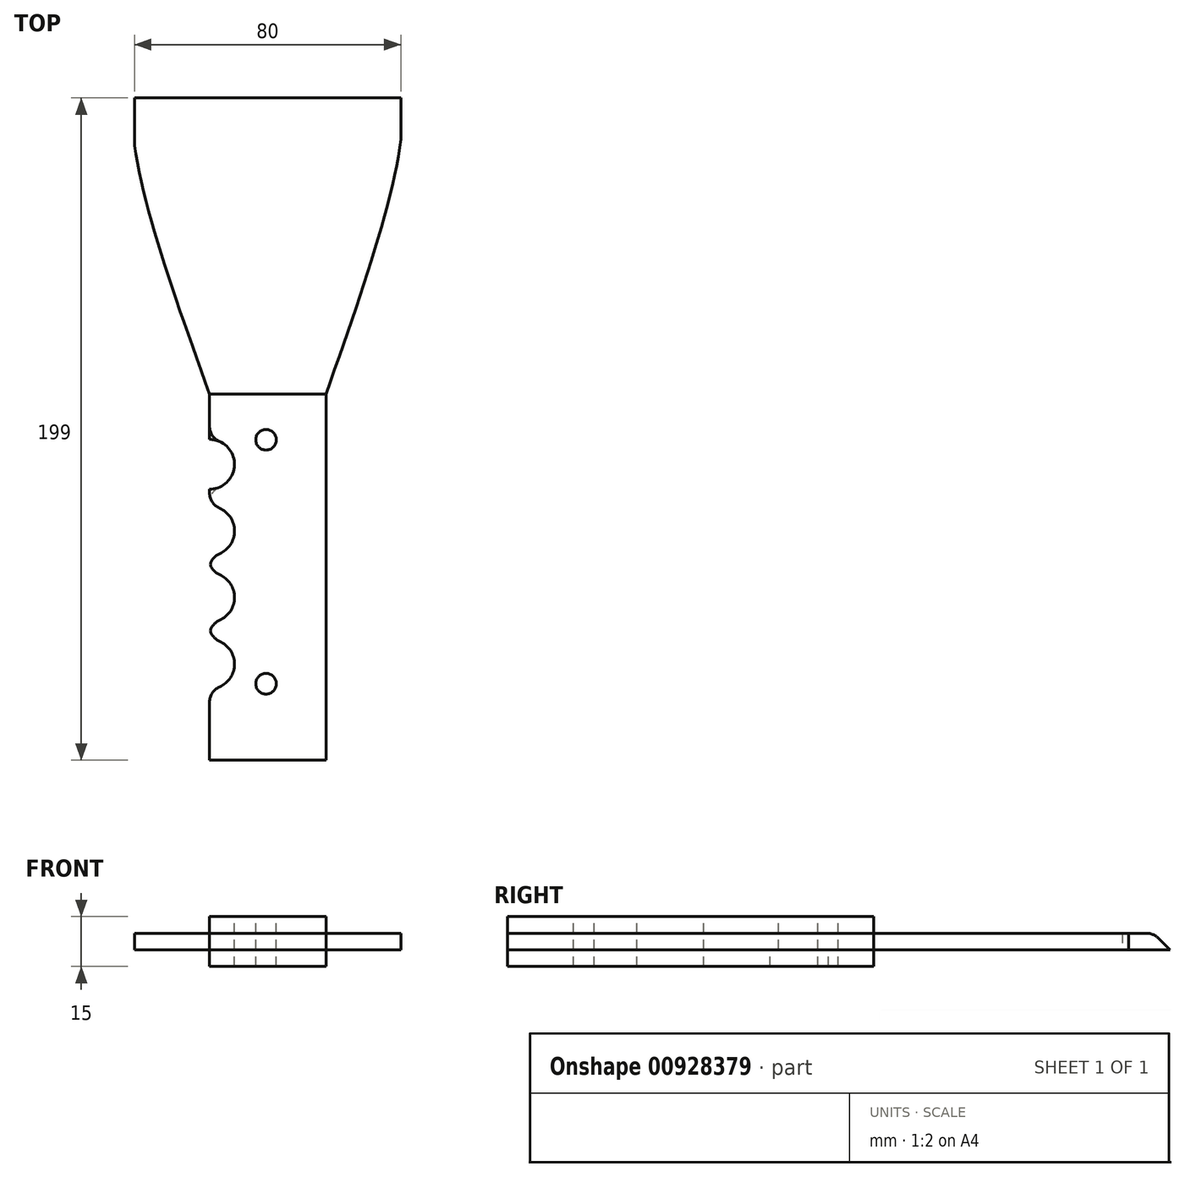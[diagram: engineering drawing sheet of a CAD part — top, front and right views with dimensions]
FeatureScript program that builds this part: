
annotation { "Feature Type Name" : "Feature", "Feature Type Description" : "" }
export const myFeature = defineFeature(function(context is Context, id is Id, definition is map)
    precondition{}
    {
        {
            var Q0;
            Q0=qCreatedBy(makeId("Top.planeOp"),FACE);
            var sketch = newSketch(context, id + "F0", { "sketchPlane" : qUnion([Q0])});
            skLineSegment(sketch, "E0.bottom", {"start": v(-27.36, -68.88) * mm, "end": v(52.64, -68.88) * mm});
            skLineSegment(sketch, "E0.top", {"start": v(-27.36, 131.12) * mm, "end": v(52.64, 131.12) * mm});
            skLineSegment(sketch, "E0.left", {"start": v(-27.36, -68.88) * mm, "end": v(-27.36, 131.12) * mm});
            skLineSegment(sketch, "E0.right", {"start": v(52.64, -68.88) * mm, "end": v(52.64, 131.12) * mm});
            skLineSegment(sketch, "E1.0", {"start": v(-27.36, 41.12) * mm, "end": v(52.64, 41.12) * mm});
            skLineSegment(sketch, "E2.0", {"start": v(30.14, -68.88) * mm, "end": v(30.14, 131.12) * mm});
            skLineSegment(sketch, "E3.0", {"start": v(-4.86, -68.88) * mm, "end": v(-4.86, 131.12) * mm});
            skFitSpline(sketch, "E4", {"points": [v(30.14, 41.12) * mm, v(52.64, 131.12) * mm, v(41.94, 146.37) * mm], "startDerivative": vector(55.76, 158.3) * mm, "endDerivative": vector(-44.94, 36.74) * mm});
            skFitSpline(sketch, "E5", {"points": [v(-4.86, 41.12) * mm, v(-27.36, 131.12) * mm, v(-15.18, 146.37) * mm], "startDerivative": vector(-57.35, 159.66) * mm, "endDerivative": vector(50, 35.48) * mm});
            skSolve(sketch);
        }
        {
            var Q0;
            {var subQ2=sQuery(id+"F0.wireOp",EDGE,"E0.top");var subQ4=sQuery(id+"F0.wireOp",EDGE,"E3.0");var subQ5=makeQuery(id+"F0.imprint","INTERSECT",VERTEX,{"derivedFrom":[subQ2,subQ4]});Q0=makeQuery(id+"F0.imprint","IMPRINT",FACE,{"disambiguationData":[TD([[makeQuery(id+"F0.imprint","IMPRINT",EDGE,{"disambiguationData":[TD([[subQ5,1.0]])],"derivedFrom":subQ2}),-1.0]])]});}
            var Q1;
            {var subQ0=sQuery(id+"F0.wireOp",EDGE,"E2.0");var subQ1=sQuery(id+"F0.wireOp",EDGE,"E0.top");var subQ2=makeQuery(id+"F0.imprint","INTERSECT",VERTEX,{"derivedFrom":[subQ1,subQ0]});Q1=makeQuery(id+"F0.imprint","IMPRINT",FACE,{"disambiguationData":[TD([[makeQuery(id+"F0.imprint","IMPRINT",EDGE,{"disambiguationData":[TD([[subQ2,1.0]])],"derivedFrom":subQ1}),-1.0]])]});}
            var Q2;
            {var subQ2=sQuery(id+"F0.wireOp",EDGE,"E0.top");var subQ4=sQuery(id+"F0.wireOp",EDGE,"E2.0");var subQ5=makeQuery(id+"F0.imprint","INTERSECT",VERTEX,{"derivedFrom":[subQ2,subQ4]});Q2=makeQuery(id+"F0.imprint","IMPRINT",FACE,{"disambiguationData":[TD([[makeQuery(id+"F0.imprint","IMPRINT",EDGE,{"disambiguationData":[TD([[subQ5,-1.0]])],"derivedFrom":subQ2}),-1.0]])]});}
            var Q3;
            {var subQ0=sQuery(id+"F0.wireOp",EDGE,"E2.0");var subQ1=sQuery(id+"F0.wireOp",EDGE,"E0.bottom");var subQ2=makeQuery(id+"F0.imprint","INTERSECT",VERTEX,{"derivedFrom":[subQ1,subQ0]});Q3=makeQuery(id+"F0.imprint","IMPRINT",FACE,{"disambiguationData":[TD([[makeQuery(id+"F0.imprint","IMPRINT",EDGE,{"disambiguationData":[TD([[subQ2,1.0]])],"derivedFrom":subQ1}),1.0]])]});}
            extrude(context, id + "F1", {"entities" : qUnion([Q0, Q1, Q2, Q3]), "depth" : 5 * mm, "offsetDistance" : 25 * mm});
        }
        {
            var Q0;
            Q0=makeQuery(id+"F1.opExtrude","CAP_FACE",FACE,{"disambiguationData":[OSD([sQuery(id+"F0.wireOp",EDGE,"E0.bottom"),sQuery(id+"F0.wireOp",EDGE,"E0.top"),sQuery(id+"F0.wireOp",EDGE,"E0.left"),sQuery(id+"F0.wireOp",EDGE,"E0.right"),sQuery(id+"F0.wireOp",EDGE,"E2.0"),sQuery(id+"F0.wireOp",EDGE,"E3.0"),sQuery(id+"F0.wireOp",EDGE,"E4"),sQuery(id+"F0.wireOp",EDGE,"E5")])],"isStart":false});
            var sketch = newSketch(context, id + "F2", { "sketchPlane" : qUnion([Q0])});
            skLineSegment(sketch, "E6", {"start": v(-4.86, 41.12) * mm, "end": v(30.14, 41.12) * mm});
            skSolve(sketch);
        }
        {
            var Q0;
            Q0=makeQuery(id+"F1.opExtrude","CAP_FACE",FACE,{"disambiguationData":[OSD([sQuery(id+"F0.wireOp",EDGE,"E0.bottom"),sQuery(id+"F0.wireOp",EDGE,"E0.top"),sQuery(id+"F0.wireOp",EDGE,"E0.left"),sQuery(id+"F0.wireOp",EDGE,"E0.right"),sQuery(id+"F0.wireOp",EDGE,"E2.0"),sQuery(id+"F0.wireOp",EDGE,"E3.0"),sQuery(id+"F0.wireOp",EDGE,"E4"),sQuery(id+"F0.wireOp",EDGE,"E5")])],"isStart":true});
            var sketch = newSketch(context, id + "F3", { "sketchPlane" : qUnion([Q0])});
            skLineSegment(sketch, "E7", {"start": v(30.14, -41.12) * mm, "end": v(-4.86, -41.12) * mm});
            skSolve(sketch);
        }
        {
            var Q0;
            Q0=makeQuery(id+"F2.imprint","IMPRINT",FACE,{"disambiguationData":[TD([[makeQuery(id+"F2.imprint","IMPRINT",EDGE,{"derivedFrom":sQuery(id+"F2.wireOp",EDGE,"E6")}),-1.0]])]});
            extrude(context, id + "F4", {"entities" : qUnion([Q0]), "depth" : 5 * mm, "offsetDistance" : 25 * mm});
        }
        {
            var Q0;
            Q0=makeQuery(id+"F3.imprint","IMPRINT",FACE,{"disambiguationData":[TD([[makeQuery(id+"F3.imprint","IMPRINT",EDGE,{"derivedFrom":sQuery(id+"F3.wireOp",EDGE,"E7")}),-1.0]])]});
            extrude(context, id + "F5", {"entities" : qUnion([Q0]), "depth" : 5 * mm, "offsetDistance" : 25 * mm});
        }
        {
            var Q0;
            Q0=makeQuery(id+"F4.opExtrude","CAP_FACE",FACE,{"disambiguationData":[OSD([sQuery(id+"F0.wireOp",EDGE,"E0.bottom"),sQuery(id+"F0.wireOp",EDGE,"E2.0"),sQuery(id+"F0.wireOp",EDGE,"E3.0"),sQuery(id+"F2.wireOp",EDGE,"E6")])],"isStart":false});
            var sketch = newSketch(context, id + "F6", { "sketchPlane" : qUnion([Q0])});
            skCircle(sketch, "E8", {"center": v(-4.86, 20) * mm, "radius": 7.5 * mm});
            skCircle(sketch, "E9", {"center": v(-4.86, 0) * mm, "radius": 7.5 * mm});
            skCircle(sketch, "E10", {"center": v(-4.86, -20) * mm, "radius": 7.5 * mm});
            skCircle(sketch, "E11", {"center": v(-4.86, -40) * mm, "radius": 7.5 * mm});
            skSolve(sketch);
        }
        {
            var Q0;
            {var subQ0=sQuery(id+"F6.wireOp",EDGE,"E8");var subQ1=makeQuery(id+"F4.opExtrude","CAP_EDGE",EDGE,{"disambiguationData":[OSD([sQuery(id+"F0.wireOp",EDGE,"E3.0")])],"isStart":false});var subQ2=makeQuery(id+"F6.imprint","INTERSECT",VERTEX,{"disambiguationData":[OD(0.0)],"derivedFrom":[subQ1,subQ0]});Q0=makeQuery(id+"F6.imprint","IMPRINT",FACE,{"disambiguationData":[TD([[makeQuery(id+"F6.imprint","IMPRINT",EDGE,{"disambiguationData":[TD([[subQ2,1.0]])],"derivedFrom":subQ0}),1.0]])]});}
            extrude(context, id + "F7", {"entities" : qUnion([Q0]), "operationType" : NewBodyOperationType.REMOVE, "oppositeDirection" : true, "depth" : 25 * mm, "offsetDistance" : 25 * mm});
        }
        {
            var Q0;
            Q0 = qSketchRegion(id + "F6", true);
            extrude(context, id + "F8", {"entities" : qUnion([Q0]), "operationType" : NewBodyOperationType.REMOVE, "oppositeDirection" : true, "depth" : 25 * mm, "offsetDistance" : 25 * mm});
        }
        {
            var Q0;
            {var subQ0=sQuery(id+"F0.wireOp",EDGE,"E3.0");var subQ1=sQuery(id+"F6.wireOp",EDGE,"E8");Q0=makeQuery(id+"F7.boolean.opBoolean","COPY",EDGE,{"disambiguationData":[topologyDisambiguationEdgeConnected([makeQuery(id+"F5.opExtrude","SWEPT_FACE",FACE,{"disambiguationData":[OSD([subQ0])]})])],"derivedFrom":makeQuery(id+"F7.opExtrude","SWEPT_EDGE",EDGE,{"disambiguationData":[OSD([subQ0,subQ1]),TDD([makeQuery(id+"F6.imprint","INTERSECT",VERTEX,{"disambiguationData":[OD(0.0)],"derivedFrom":[makeQuery(id+"F4.opExtrude","CAP_EDGE",EDGE,{"disambiguationData":[OSD([subQ0])],"isStart":false}),subQ1]})])]})});}
            var Q1;
            {var subQ0=sQuery(id+"F0.wireOp",EDGE,"E3.0");var subQ1=sQuery(id+"F6.wireOp",EDGE,"E8");Q1=makeQuery(id+"F7.boolean.opBoolean","COPY",EDGE,{"disambiguationData":[topologyDisambiguationEdgeConnected([makeQuery(id+"F1.opExtrude","SWEPT_FACE",FACE,{"disambiguationData":[OSD([subQ0])]})])],"derivedFrom":makeQuery(id+"F7.opExtrude","SWEPT_EDGE",EDGE,{"disambiguationData":[OSD([subQ0,subQ1]),TDD([makeQuery(id+"F6.imprint","INTERSECT",VERTEX,{"disambiguationData":[OD(0.0)],"derivedFrom":[makeQuery(id+"F4.opExtrude","CAP_EDGE",EDGE,{"disambiguationData":[OSD([subQ0])],"isStart":false}),subQ1]})])]})});}
            var Q2;
            {var subQ0=sQuery(id+"F0.wireOp",EDGE,"E3.0");var subQ1=sQuery(id+"F6.wireOp",EDGE,"E8");Q2=makeQuery(id+"F7.boolean.opBoolean","COPY",EDGE,{"disambiguationData":[topologyDisambiguationEdgeConnected([makeQuery(id+"F4.opExtrude","SWEPT_FACE",FACE,{"disambiguationData":[OSD([subQ0])]})])],"derivedFrom":makeQuery(id+"F7.opExtrude","SWEPT_EDGE",EDGE,{"disambiguationData":[OSD([subQ0,subQ1]),TDD([makeQuery(id+"F6.imprint","INTERSECT",VERTEX,{"disambiguationData":[OD(0.0)],"derivedFrom":[makeQuery(id+"F4.opExtrude","CAP_EDGE",EDGE,{"disambiguationData":[OSD([subQ0])],"isStart":false}),subQ1]})])]})});}
            var Q3;
            {var subQ0=sQuery(id+"F0.wireOp",EDGE,"E3.0");var subQ1=sQuery(id+"F6.wireOp",EDGE,"E8");Q3=makeQuery(id+"F7.boolean.opBoolean","COPY",EDGE,{"disambiguationData":[topologyDisambiguationEdgeConnected([makeQuery(id+"F1.opExtrude","SWEPT_FACE",FACE,{"disambiguationData":[OSD([subQ0])]})])],"derivedFrom":makeQuery(id+"F7.opExtrude","SWEPT_EDGE",EDGE,{"disambiguationData":[OSD([subQ0,subQ1]),TDD([makeQuery(id+"F6.imprint","INTERSECT",VERTEX,{"disambiguationData":[OD(1.0)],"derivedFrom":[makeQuery(id+"F4.opExtrude","CAP_EDGE",EDGE,{"disambiguationData":[OSD([subQ0])],"isStart":false}),subQ1]})])]})});}
            var Q4;
            {var subQ0=sQuery(id+"F0.wireOp",EDGE,"E3.0");var subQ1=sQuery(id+"F6.wireOp",EDGE,"E8");Q4=makeQuery(id+"F7.boolean.opBoolean","COPY",EDGE,{"disambiguationData":[topologyDisambiguationEdgeConnected([makeQuery(id+"F4.opExtrude","SWEPT_FACE",FACE,{"disambiguationData":[OSD([subQ0])]})])],"derivedFrom":makeQuery(id+"F7.opExtrude","SWEPT_EDGE",EDGE,{"disambiguationData":[OSD([subQ0,subQ1]),TDD([makeQuery(id+"F6.imprint","INTERSECT",VERTEX,{"disambiguationData":[OD(1.0)],"derivedFrom":[makeQuery(id+"F4.opExtrude","CAP_EDGE",EDGE,{"disambiguationData":[OSD([subQ0])],"isStart":false}),subQ1]})])]})});}
            var Q5;
            {var subQ0=sQuery(id+"F0.wireOp",EDGE,"E3.0");var subQ1=sQuery(id+"F6.wireOp",EDGE,"E8");Q5=makeQuery(id+"F7.boolean.opBoolean","COPY",EDGE,{"disambiguationData":[topologyDisambiguationEdgeConnected([makeQuery(id+"F5.opExtrude","SWEPT_FACE",FACE,{"disambiguationData":[OSD([subQ0])]})])],"derivedFrom":makeQuery(id+"F7.opExtrude","SWEPT_EDGE",EDGE,{"disambiguationData":[OSD([subQ0,subQ1]),TDD([makeQuery(id+"F6.imprint","INTERSECT",VERTEX,{"disambiguationData":[OD(1.0)],"derivedFrom":[makeQuery(id+"F4.opExtrude","CAP_EDGE",EDGE,{"disambiguationData":[OSD([subQ0])],"isStart":false}),subQ1]})])]})});}
            var Q6;
            {var subQ1=sQuery(id+"F0.wireOp",EDGE,"E3.0");var subQ3=sQuery(id+"F0.wireOp",EDGE,"E0.bottom");Q6=makeQuery(id+"F8.boolean.opBoolean","INTERSECT",EDGE,{"disambiguationData":[OD(0.0)],"derivedFrom":[makeQuery(id+"F7.boolean.opBoolean","SPLIT",FACE,{"disambiguationData":[TD([makeQuery(id+"F5.opExtrude","SWEPT_FACE",FACE,{"disambiguationData":[OSD([subQ3])]})])],"derivedFrom":makeQuery(id+"F5.opExtrude","SWEPT_FACE",FACE,{"disambiguationData":[OSD([subQ1])]})}),makeQuery(id+"F8.opExtrude","SWEPT_FACE",FACE,{"disambiguationData":[OSD([sQuery(id+"F6.wireOp",EDGE,"E9")])]})]});}
            var Q7;
            {var subQ0=sQuery(id+"F0.wireOp",EDGE,"E0.bottom");var subQ3=sQuery(id+"F0.wireOp",EDGE,"E3.0");Q7=makeQuery(id+"F8.boolean.opBoolean","INTERSECT",EDGE,{"disambiguationData":[OD(0.0)],"derivedFrom":[makeQuery(id+"F7.boolean.opBoolean","SPLIT",FACE,{"disambiguationData":[TD([makeQuery(id+"F1.opExtrude","SWEPT_FACE",FACE,{"disambiguationData":[OSD([subQ0])]})])],"derivedFrom":makeQuery(id+"F1.opExtrude","SWEPT_FACE",FACE,{"disambiguationData":[OSD([subQ3])]})}),makeQuery(id+"F8.opExtrude","SWEPT_FACE",FACE,{"disambiguationData":[OSD([sQuery(id+"F6.wireOp",EDGE,"E9")])]})]});}
            var Q8;
            {var subQ1=sQuery(id+"F0.wireOp",EDGE,"E3.0");var subQ3=sQuery(id+"F0.wireOp",EDGE,"E0.bottom");Q8=makeQuery(id+"F8.boolean.opBoolean","INTERSECT",EDGE,{"disambiguationData":[OD(0.0)],"derivedFrom":[makeQuery(id+"F7.boolean.opBoolean","SPLIT",FACE,{"disambiguationData":[TD([makeQuery(id+"F4.opExtrude","SWEPT_FACE",FACE,{"disambiguationData":[OSD([subQ3])]})])],"derivedFrom":makeQuery(id+"F4.opExtrude","SWEPT_FACE",FACE,{"disambiguationData":[OSD([subQ1])]})}),makeQuery(id+"F8.opExtrude","SWEPT_FACE",FACE,{"disambiguationData":[OSD([sQuery(id+"F6.wireOp",EDGE,"E9")])]})]});}
            var Q9;
            {var subQ0=sQuery(id+"F0.wireOp",EDGE,"E0.bottom");var subQ3=sQuery(id+"F0.wireOp",EDGE,"E3.0");Q9=makeQuery(id+"F8.boolean.opBoolean","INTERSECT",EDGE,{"disambiguationData":[OD(0.0)],"derivedFrom":[makeQuery(id+"F7.boolean.opBoolean","SPLIT",FACE,{"disambiguationData":[TD([makeQuery(id+"F1.opExtrude","SWEPT_FACE",FACE,{"disambiguationData":[OSD([subQ0])]})])],"derivedFrom":makeQuery(id+"F1.opExtrude","SWEPT_FACE",FACE,{"disambiguationData":[OSD([subQ3])]})}),makeQuery(id+"F8.opExtrude","SWEPT_FACE",FACE,{"disambiguationData":[OSD([sQuery(id+"F6.wireOp",EDGE,"E10")])]})]});}
            var Q10;
            {var subQ1=sQuery(id+"F0.wireOp",EDGE,"E3.0");var subQ3=sQuery(id+"F0.wireOp",EDGE,"E0.bottom");Q10=makeQuery(id+"F8.boolean.opBoolean","INTERSECT",EDGE,{"disambiguationData":[OD(0.0)],"derivedFrom":[makeQuery(id+"F7.boolean.opBoolean","SPLIT",FACE,{"disambiguationData":[TD([makeQuery(id+"F5.opExtrude","SWEPT_FACE",FACE,{"disambiguationData":[OSD([subQ3])]})])],"derivedFrom":makeQuery(id+"F5.opExtrude","SWEPT_FACE",FACE,{"disambiguationData":[OSD([subQ1])]})}),makeQuery(id+"F8.opExtrude","SWEPT_FACE",FACE,{"disambiguationData":[OSD([sQuery(id+"F6.wireOp",EDGE,"E10")])]})]});}
            var Q11;
            {var subQ1=sQuery(id+"F0.wireOp",EDGE,"E3.0");var subQ3=sQuery(id+"F0.wireOp",EDGE,"E0.bottom");Q11=makeQuery(id+"F8.boolean.opBoolean","INTERSECT",EDGE,{"disambiguationData":[OD(0.0)],"derivedFrom":[makeQuery(id+"F7.boolean.opBoolean","SPLIT",FACE,{"disambiguationData":[TD([makeQuery(id+"F4.opExtrude","SWEPT_FACE",FACE,{"disambiguationData":[OSD([subQ3])]})])],"derivedFrom":makeQuery(id+"F4.opExtrude","SWEPT_FACE",FACE,{"disambiguationData":[OSD([subQ1])]})}),makeQuery(id+"F8.opExtrude","SWEPT_FACE",FACE,{"disambiguationData":[OSD([sQuery(id+"F6.wireOp",EDGE,"E10")])]})]});}
            var Q12;
            {var subQ1=sQuery(id+"F0.wireOp",EDGE,"E3.0");var subQ3=sQuery(id+"F0.wireOp",EDGE,"E0.bottom");Q12=makeQuery(id+"F8.boolean.opBoolean","INTERSECT",EDGE,{"disambiguationData":[OD(1.0)],"derivedFrom":[makeQuery(id+"F7.boolean.opBoolean","SPLIT",FACE,{"disambiguationData":[TD([makeQuery(id+"F4.opExtrude","SWEPT_FACE",FACE,{"disambiguationData":[OSD([subQ3])]})])],"derivedFrom":makeQuery(id+"F4.opExtrude","SWEPT_FACE",FACE,{"disambiguationData":[OSD([subQ1])]})}),makeQuery(id+"F8.opExtrude","SWEPT_FACE",FACE,{"disambiguationData":[OSD([sQuery(id+"F6.wireOp",EDGE,"E9")])]})]});}
            var Q13;
            {var subQ0=sQuery(id+"F0.wireOp",EDGE,"E0.bottom");var subQ3=sQuery(id+"F0.wireOp",EDGE,"E3.0");Q13=makeQuery(id+"F8.boolean.opBoolean","INTERSECT",EDGE,{"disambiguationData":[OD(1.0)],"derivedFrom":[makeQuery(id+"F7.boolean.opBoolean","SPLIT",FACE,{"disambiguationData":[TD([makeQuery(id+"F1.opExtrude","SWEPT_FACE",FACE,{"disambiguationData":[OSD([subQ0])]})])],"derivedFrom":makeQuery(id+"F1.opExtrude","SWEPT_FACE",FACE,{"disambiguationData":[OSD([subQ3])]})}),makeQuery(id+"F8.opExtrude","SWEPT_FACE",FACE,{"disambiguationData":[OSD([sQuery(id+"F6.wireOp",EDGE,"E9")])]})]});}
            var Q14;
            {var subQ1=sQuery(id+"F0.wireOp",EDGE,"E3.0");var subQ3=sQuery(id+"F0.wireOp",EDGE,"E0.bottom");Q14=makeQuery(id+"F8.boolean.opBoolean","INTERSECT",EDGE,{"disambiguationData":[OD(1.0)],"derivedFrom":[makeQuery(id+"F7.boolean.opBoolean","SPLIT",FACE,{"disambiguationData":[TD([makeQuery(id+"F5.opExtrude","SWEPT_FACE",FACE,{"disambiguationData":[OSD([subQ3])]})])],"derivedFrom":makeQuery(id+"F5.opExtrude","SWEPT_FACE",FACE,{"disambiguationData":[OSD([subQ1])]})}),makeQuery(id+"F8.opExtrude","SWEPT_FACE",FACE,{"disambiguationData":[OSD([sQuery(id+"F6.wireOp",EDGE,"E9")])]})]});}
            var Q15;
            {var subQ1=sQuery(id+"F0.wireOp",EDGE,"E3.0");var subQ3=sQuery(id+"F0.wireOp",EDGE,"E0.bottom");Q15=makeQuery(id+"F8.boolean.opBoolean","INTERSECT",EDGE,{"disambiguationData":[OD(1.0)],"derivedFrom":[makeQuery(id+"F7.boolean.opBoolean","SPLIT",FACE,{"disambiguationData":[TD([makeQuery(id+"F5.opExtrude","SWEPT_FACE",FACE,{"disambiguationData":[OSD([subQ3])]})])],"derivedFrom":makeQuery(id+"F5.opExtrude","SWEPT_FACE",FACE,{"disambiguationData":[OSD([subQ1])]})}),makeQuery(id+"F8.opExtrude","SWEPT_FACE",FACE,{"disambiguationData":[OSD([sQuery(id+"F6.wireOp",EDGE,"E11")])]})]});}
            var Q16;
            {var subQ0=sQuery(id+"F0.wireOp",EDGE,"E0.bottom");var subQ3=sQuery(id+"F0.wireOp",EDGE,"E3.0");Q16=makeQuery(id+"F8.boolean.opBoolean","INTERSECT",EDGE,{"disambiguationData":[OD(1.0)],"derivedFrom":[makeQuery(id+"F7.boolean.opBoolean","SPLIT",FACE,{"disambiguationData":[TD([makeQuery(id+"F1.opExtrude","SWEPT_FACE",FACE,{"disambiguationData":[OSD([subQ0])]})])],"derivedFrom":makeQuery(id+"F1.opExtrude","SWEPT_FACE",FACE,{"disambiguationData":[OSD([subQ3])]})}),makeQuery(id+"F8.opExtrude","SWEPT_FACE",FACE,{"disambiguationData":[OSD([sQuery(id+"F6.wireOp",EDGE,"E11")])]})]});}
            var Q17;
            {var subQ1=sQuery(id+"F0.wireOp",EDGE,"E3.0");var subQ3=sQuery(id+"F0.wireOp",EDGE,"E0.bottom");Q17=makeQuery(id+"F8.boolean.opBoolean","INTERSECT",EDGE,{"disambiguationData":[OD(1.0)],"derivedFrom":[makeQuery(id+"F7.boolean.opBoolean","SPLIT",FACE,{"disambiguationData":[TD([makeQuery(id+"F4.opExtrude","SWEPT_FACE",FACE,{"disambiguationData":[OSD([subQ3])]})])],"derivedFrom":makeQuery(id+"F4.opExtrude","SWEPT_FACE",FACE,{"disambiguationData":[OSD([subQ1])]})}),makeQuery(id+"F8.opExtrude","SWEPT_FACE",FACE,{"disambiguationData":[OSD([sQuery(id+"F6.wireOp",EDGE,"E11")])]})]});}
            var Q18;
            {var subQ1=sQuery(id+"F0.wireOp",EDGE,"E3.0");var subQ3=sQuery(id+"F0.wireOp",EDGE,"E0.bottom");Q18=makeQuery(id+"F8.boolean.opBoolean","INTERSECT",EDGE,{"disambiguationData":[OD(1.0)],"derivedFrom":[makeQuery(id+"F7.boolean.opBoolean","SPLIT",FACE,{"disambiguationData":[TD([makeQuery(id+"F4.opExtrude","SWEPT_FACE",FACE,{"disambiguationData":[OSD([subQ3])]})])],"derivedFrom":makeQuery(id+"F4.opExtrude","SWEPT_FACE",FACE,{"disambiguationData":[OSD([subQ1])]})}),makeQuery(id+"F8.opExtrude","SWEPT_FACE",FACE,{"disambiguationData":[OSD([sQuery(id+"F6.wireOp",EDGE,"E10")])]})]});}
            var Q19;
            {var subQ0=sQuery(id+"F0.wireOp",EDGE,"E0.bottom");var subQ3=sQuery(id+"F0.wireOp",EDGE,"E3.0");Q19=makeQuery(id+"F8.boolean.opBoolean","INTERSECT",EDGE,{"disambiguationData":[OD(1.0)],"derivedFrom":[makeQuery(id+"F7.boolean.opBoolean","SPLIT",FACE,{"disambiguationData":[TD([makeQuery(id+"F1.opExtrude","SWEPT_FACE",FACE,{"disambiguationData":[OSD([subQ0])]})])],"derivedFrom":makeQuery(id+"F1.opExtrude","SWEPT_FACE",FACE,{"disambiguationData":[OSD([subQ3])]})}),makeQuery(id+"F8.opExtrude","SWEPT_FACE",FACE,{"disambiguationData":[OSD([sQuery(id+"F6.wireOp",EDGE,"E10")])]})]});}
            var Q20;
            {var subQ1=sQuery(id+"F0.wireOp",EDGE,"E3.0");var subQ3=sQuery(id+"F0.wireOp",EDGE,"E0.bottom");Q20=makeQuery(id+"F8.boolean.opBoolean","INTERSECT",EDGE,{"disambiguationData":[OD(1.0)],"derivedFrom":[makeQuery(id+"F7.boolean.opBoolean","SPLIT",FACE,{"disambiguationData":[TD([makeQuery(id+"F5.opExtrude","SWEPT_FACE",FACE,{"disambiguationData":[OSD([subQ3])]})])],"derivedFrom":makeQuery(id+"F5.opExtrude","SWEPT_FACE",FACE,{"disambiguationData":[OSD([subQ1])]})}),makeQuery(id+"F8.opExtrude","SWEPT_FACE",FACE,{"disambiguationData":[OSD([sQuery(id+"F6.wireOp",EDGE,"E10")])]})]});}
            var Q21;
            {var subQ1=sQuery(id+"F0.wireOp",EDGE,"E3.0");var subQ3=sQuery(id+"F0.wireOp",EDGE,"E0.bottom");Q21=makeQuery(id+"F8.boolean.opBoolean","INTERSECT",EDGE,{"disambiguationData":[OD(0.0)],"derivedFrom":[makeQuery(id+"F7.boolean.opBoolean","SPLIT",FACE,{"disambiguationData":[TD([makeQuery(id+"F4.opExtrude","SWEPT_FACE",FACE,{"disambiguationData":[OSD([subQ3])]})])],"derivedFrom":makeQuery(id+"F4.opExtrude","SWEPT_FACE",FACE,{"disambiguationData":[OSD([subQ1])]})}),makeQuery(id+"F8.opExtrude","SWEPT_FACE",FACE,{"disambiguationData":[OSD([sQuery(id+"F6.wireOp",EDGE,"E11")])]})]});}
            var Q22;
            {var subQ0=sQuery(id+"F0.wireOp",EDGE,"E0.bottom");var subQ3=sQuery(id+"F0.wireOp",EDGE,"E3.0");Q22=makeQuery(id+"F8.boolean.opBoolean","INTERSECT",EDGE,{"disambiguationData":[OD(0.0)],"derivedFrom":[makeQuery(id+"F7.boolean.opBoolean","SPLIT",FACE,{"disambiguationData":[TD([makeQuery(id+"F1.opExtrude","SWEPT_FACE",FACE,{"disambiguationData":[OSD([subQ0])]})])],"derivedFrom":makeQuery(id+"F1.opExtrude","SWEPT_FACE",FACE,{"disambiguationData":[OSD([subQ3])]})}),makeQuery(id+"F8.opExtrude","SWEPT_FACE",FACE,{"disambiguationData":[OSD([sQuery(id+"F6.wireOp",EDGE,"E11")])]})]});}
            var Q23;
            {var subQ1=sQuery(id+"F0.wireOp",EDGE,"E3.0");var subQ3=sQuery(id+"F0.wireOp",EDGE,"E0.bottom");Q23=makeQuery(id+"F8.boolean.opBoolean","INTERSECT",EDGE,{"disambiguationData":[OD(0.0)],"derivedFrom":[makeQuery(id+"F7.boolean.opBoolean","SPLIT",FACE,{"disambiguationData":[TD([makeQuery(id+"F5.opExtrude","SWEPT_FACE",FACE,{"disambiguationData":[OSD([subQ3])]})])],"derivedFrom":makeQuery(id+"F5.opExtrude","SWEPT_FACE",FACE,{"disambiguationData":[OSD([subQ1])]})}),makeQuery(id+"F8.opExtrude","SWEPT_FACE",FACE,{"disambiguationData":[OSD([sQuery(id+"F6.wireOp",EDGE,"E11")])]})]});}
            fillet(context, id + "F9", {"entities" : qUnion([Q0, Q1, Q2, Q3, Q4, Q5, Q6, Q7, Q8, Q9, Q10, Q11, Q12, Q13, Q14, Q15, Q16, Q17, Q18, Q19, Q20, Q21, Q22, Q23]), "radius" : 5 * mm, "tangentPropagation" : true, "allowEdgeOverflow" : false});
        }
        {
            var Q0;
            Q0=makeQuery(id+"F4.opExtrude","CAP_FACE",FACE,{"disambiguationData":[OSD([sQuery(id+"F0.wireOp",EDGE,"E0.bottom"),sQuery(id+"F0.wireOp",EDGE,"E2.0"),sQuery(id+"F0.wireOp",EDGE,"E3.0"),sQuery(id+"F2.wireOp",EDGE,"E6")])],"isStart":false});
            var sketch = newSketch(context, id + "F10", { "sketchPlane" : qUnion([Q0])});
            skCircle(sketch, "E12", {"center": v(12.13, 27.4) * mm, "radius": 3.1 * mm});
            skCircle(sketch, "E13", {"center": v(12.13, -45.9) * mm, "radius": 3.1 * mm});
            skSolve(sketch);
        }
        {
            var Q0;
            Q0=makeQuery(id+"F10.imprint","IMPRINT",FACE,{"disambiguationData":[TD([[makeQuery(id+"F10.imprint","IMPRINT",EDGE,{"derivedFrom":sQuery(id+"F10.wireOp",EDGE,"E12")}),1.0]])]});
            extrude(context, id + "F11", {"entities" : qUnion([Q0]), "operationType" : NewBodyOperationType.REMOVE, "oppositeDirection" : true, "depth" : 25 * mm, "offsetDistance" : 25 * mm});
        }
        {
            var Q0;
            Q0 = qSketchRegion(id + "F10", true);
            extrude(context, id + "F12", {"entities" : qUnion([Q0]), "operationType" : NewBodyOperationType.REMOVE, "oppositeDirection" : true, "depth" : 25 * mm, "offsetDistance" : 25 * mm});
        }
        {
            var Q0;
            Q0=makeQuery(id+"F1.opExtrude","CAP_EDGE",EDGE,{"disambiguationData":[OSD([sQuery(id+"F0.wireOp",EDGE,"E0.top")])],"isStart":false});
            chamfer(context, id + "F13", {"entities" : qUnion([Q0]), "width" : 6 * mm, "tangentPropagation" : true});
        }
        {
            var Q0;
            {var subQ0=sQuery(id+"F0.wireOp",EDGE,"E0.top");Q0=makeQuery(id+"F13.opChamfer","BLEND_EDGE",EDGE,{"blendedFrom":[makeQuery(id+"F1.opExtrude","CAP_EDGE",EDGE,{"disambiguationData":[OSD([subQ0])],"isStart":false}),makeQuery(id+"F1.opExtrude","CAP_FACE",FACE,{"disambiguationData":[OSD([sQuery(id+"F0.wireOp",EDGE,"E0.bottom"),subQ0,sQuery(id+"F0.wireOp",EDGE,"E0.left"),sQuery(id+"F0.wireOp",EDGE,"E0.right"),sQuery(id+"F0.wireOp",EDGE,"E2.0"),sQuery(id+"F0.wireOp",EDGE,"E3.0"),sQuery(id+"F0.wireOp",EDGE,"E4"),sQuery(id+"F0.wireOp",EDGE,"E5")])],"isStart":false})],"blendedInto":[makeQuery(id+"F1.opExtrude","CAP_FACE",FACE,{"disambiguationData":[OSD([sQuery(id+"F0.wireOp",EDGE,"E0.bottom"),subQ0,sQuery(id+"F0.wireOp",EDGE,"E0.left"),sQuery(id+"F0.wireOp",EDGE,"E0.right"),sQuery(id+"F0.wireOp",EDGE,"E2.0"),sQuery(id+"F0.wireOp",EDGE,"E3.0"),sQuery(id+"F0.wireOp",EDGE,"E4"),sQuery(id+"F0.wireOp",EDGE,"E5")])],"isStart":false})]});}
            fillet(context, id + "F14", {"entities" : qUnion([Q0]), "radius" : 5 * mm, "tangentPropagation" : true, "allowEdgeOverflow" : false});
        }
    });
